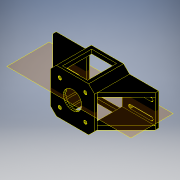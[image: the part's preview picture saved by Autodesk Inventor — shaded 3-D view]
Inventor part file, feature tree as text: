
AUTODESK INVENTOR PART (.ipt)
format: ipt  version: 2016 (Build 200138000, 138)  size: 540,672 bytes
history: native  units: in
note: dims shown in document units (in); Inventor stores cm internally (conversion verified against a paired STEP export)
features: other x3, plane x1
ambient origin geometry x8: Origin, YZ Plane, XZ Plane, XY Plane, X Axis, Y Axis, Z Axis, Center Point
bodies: Body1 (feature_tree)
feature tree (4):
  other  "rotating_table_motor_holder"
  plane  "Work Plane1"
  other  "Composite1"
  other  "Srf1"
